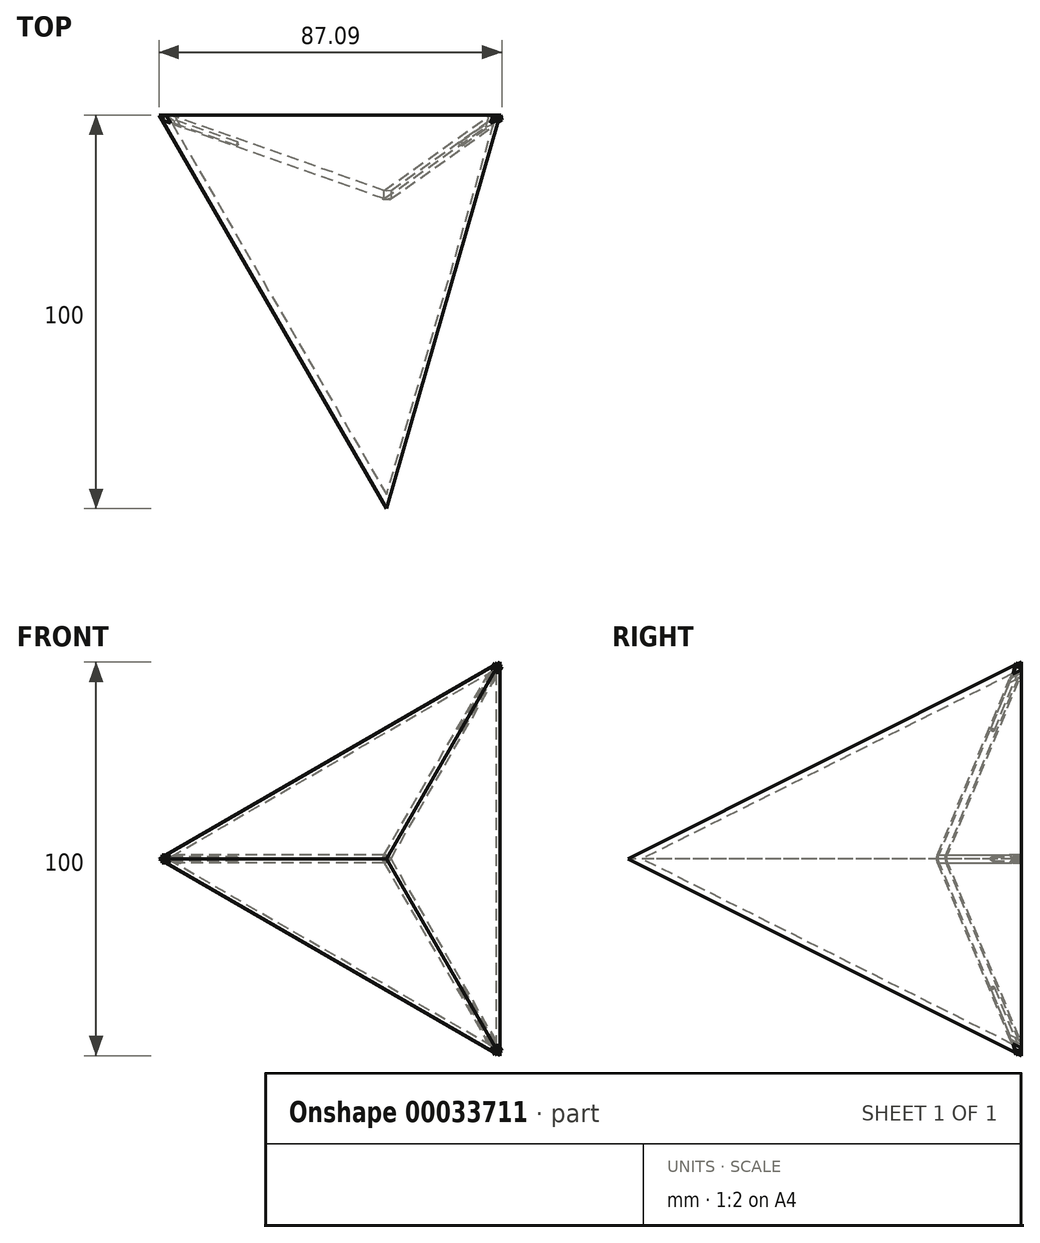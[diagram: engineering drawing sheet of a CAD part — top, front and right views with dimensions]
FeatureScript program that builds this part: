
annotation { "Feature Type Name" : "Feature", "Feature Type Description" : "" }
export const myFeature = defineFeature(function(context is Context, id is Id, definition is map)
    precondition{}
    {
        {
            var Q0;
            Q0=qCreatedBy(makeId("Front.planeOp"),FACE);
            var sketch = newSketch(context, id + "F0", { "sketchPlane" : qUnion([Q0])});
            skCircle(sketch, "E0.cCircle", {"center": v(0, 0) * mm, "radius": 28.87 * mm, "construction": true});
            skLineSegment(sketch, "E0.0", {"start": v(28.87, 50) * mm, "end": v(28.87, -50) * mm});
            skLineSegment(sketch, "E0.1", {"start": v(28.87, -50) * mm, "end": v(-57.74, 0) * mm});
            skLineSegment(sketch, "E0.2", {"start": v(-57.74, 0) * mm, "end": v(28.87, 50) * mm});
            skPoint(sketch, "E0.0.midPoint", {"position": v(28.87, 0) * mm});
            skSolve(sketch);
        }
        {
            var Q0;
            Q0=makeQuery(id+"F0.imprint","IMPRINT",FACE,{"disambiguationData":[TD([[makeQuery(id+"F0.imprint","IMPRINT",EDGE,{"derivedFrom":sQuery(id+"F0.wireOp",EDGE,"E0.0")}),-1.0]])]});
            cPlane(context, id + "F1", {"entities" : qUnion([Q0]), "cplaneType" : CPlaneType.OFFSET, "offset" : 100 * mm, "width" : 150 * mm, "height" : 150 * mm});
        }
        {
            var Q0;
            Q0=qCreatedBy(id+"F1.planeOp",FACE);
            var sketch = newSketch(context, id + "F2", { "sketchPlane" : qUnion([Q0])});
            skPoint(sketch, "E1", {"position": v(0, 0) * mm});
            skSolve(sketch);
        }
        {
            var Q0;
            Q0=makeQuery(id+"F0.imprint","IMPRINT",FACE,{"disambiguationData":[TD([[makeQuery(id+"F0.imprint","IMPRINT",EDGE,{"derivedFrom":sQuery(id+"F0.wireOp",EDGE,"E0.0")}),-1.0]])]});
            var Q1;
            Q1=sQuery(id+"F2.wireOp",VERTEX,"E1");
            loft(context, id + "F3", {"sheetProfilesArray" : [{ "sheetProfileEntities" : qUnion([Q0]) }, { "sheetProfileEntities" : qUnion([Q1]) }]});
        }
        {
            var Q0;
            Q0=makeQuery(id+"F3.opLoft","CAP_FACE",FACE,{"disambiguationData":[OSD([makeQuery(id+"F0.imprint","IMPRINT",FACE,{"disambiguationData":[TD([[makeQuery(id+"F0.imprint","IMPRINT",EDGE,{"derivedFrom":sQuery(id+"F0.wireOp",EDGE,"E0.0")}),-1.0]])]})])],"isStart":true});
            shell(context, id + "F4", {"entities" : qUnion([Q0]), "thickness" : 1 * mm});
        }
        {
            var Q0;
            Q0=qCreatedBy(makeId("Top.planeOp"),FACE);
            var sketch = newSketch(context, id + "F5", { "sketchPlane" : qUnion([Q0])});
            skLineSegment(sketch, "E2.0.0", {"start": v(-57.74, 0) * mm, "end": v(0, -100) * mm});
            skLineSegment(sketch, "E2.0.1", {"start": v(0, -100) * mm, "end": v(28.87, 0) * mm});
            skLineSegment(sketch, "E2.0.2", {"start": v(28.87, 0) * mm, "end": v(-57.74, 0) * mm});
            skLineSegment(sketch, "E3", {"start": v(0, -100) * mm, "end": v(0, 0) * mm});
            skLineSegment(sketch, "E4", {"start": v(-57.74, 0) * mm, "end": v(0, -20.45) * mm});
            skPoint(sketch, "E5", {"position": v(-57.74, 0) * mm});
            skLineSegment(sketch, "E6", {"start": v(0, -19.38) * mm, "end": v(-54.74, 0) * mm});
            skLineSegment(sketch, "E7", {"start": v(0, -21.5) * mm, "end": v(-56.97, -1.33) * mm});
            skSolve(sketch);
        }
        {
            var Q0;
            {var subQ0=sQuery(id+"F5.wireOp",EDGE,"E4");Q0=makeQuery(id+"F5.imprint","IMPRINT",FACE,{"disambiguationData":[TD([[makeQuery(id+"F5.imprint","IMPRINT",EDGE,{"derivedFrom":subQ0}),1.0]])]});}
            var Q1;
            {var subQ0=sQuery(id+"F5.wireOp",EDGE,"E4");Q1=makeQuery(id+"F5.imprint","IMPRINT",FACE,{"disambiguationData":[TD([[makeQuery(id+"F5.imprint","IMPRINT",EDGE,{"derivedFrom":subQ0}),-1.0]])]});}
            extrude(context, id + "F6", {"entities" : qUnion([Q0, Q1]), "operationType" : NewBodyOperationType.ADD, "depth" : 1 * mm, "hasSecondDirection" : true, "secondDirectionOppositeDirection" : true, "secondDirectionDepth" : 1 * mm});
        }
        {
            var Q0;
            {var subQ0=sQuery(id+"F5.wireOp",EDGE,"E2.0.2");var subQ1=sQuery(id+"F5.wireOp",EDGE,"E2.0.0");var subQ6=sQuery(id+"F5.wireOp",EDGE,"E7");Q0=makeQuery(id+"F6.boolean.opBoolean","SPLIT",FACE,{"disambiguationData":[TD([makeQuery(id+"F6.opExtrude","SWEPT_FACE",FACE,{"disambiguationData":[OSD([subQ1])]})])],"derivedFrom":makeQuery(id+"F6.opExtrude","CAP_FACE",FACE,{"disambiguationData":[OSD([subQ1,subQ0,sQuery(id+"F5.wireOp",EDGE,"E3"),sQuery(id+"F5.wireOp",EDGE,"E6"),subQ6])],"isStart":false})});}
            var sketch = newSketch(context, id + "F7", { "sketchPlane" : qUnion([Q0])});
            skLineSegment(sketch, "E8", {"start": v(-56.97, -1.33) * mm, "end": v(-56.5, 0) * mm});
            skLineSegment(sketch, "E9.0", {"start": v(0, -19.38) * mm, "end": v(-53.71, -0.36) * mm});
            skSolve(sketch);
        }
        {
            var Q0;
            {var subQ0=sQuery(id+"F7.wireOp",EDGE,"E8");Q0=makeQuery(id+"F7.imprint","IMPRINT",FACE,{"disambiguationData":[TD([[makeQuery(id+"F7.imprint","IMPRINT",EDGE,{"derivedFrom":subQ0}),1.0]])]});}
            extrude(context, id + "F8", {"entities" : qUnion([Q0]), "operationType" : NewBodyOperationType.REMOVE, "endBound" : BoundingType.THROUGH_ALL, "oppositeDirection" : true, "depth" : 25 * mm});
        }
        {
            var Q0;
            Q0=makeQuery(id+"F8.boolean.opBoolean","COPY",FACE,{"derivedFrom":makeQuery(id+"F8.opExtrude","SWEPT_FACE",FACE,{"disambiguationData":[OSD([sQuery(id+"F7.wireOp",EDGE,"E8")])]})});
            var sketch = newSketch(context, id + "F9", { "sketchPlane" : qUnion([Q0])});
            skLineSegment(sketch, "E10.0.0", {"start": v(20.27, -1) * mm, "end": v(20.27, 0) * mm});
            skLineSegment(sketch, "E10.0.1", {"start": v(20.27, 0) * mm, "end": v(20.27, 1) * mm});
            skLineSegment(sketch, "E10.0.2", {"start": v(20.27, 1) * mm, "end": v(18.86, 1) * mm});
            skLineSegment(sketch, "E10.0.3", {"start": v(18.86, 1) * mm, "end": v(18.86, -1) * mm});
            skLineSegment(sketch, "E10.0.4", {"start": v(18.86, -1) * mm, "end": v(20.27, -1) * mm});
            skPoint(sketch, "E11", {"position": v(19.57, 0) * mm});
            skSolve(sketch);
        }
        {
            var Q0;
            Q0=sQuery(id+"F9.wireOp",VERTEX,"E11");
            var Q1;
            Q1=makeQuery(id+"F3.opLoft","SWEPT_BODY",BODY,{"disambiguationData":[OSD([makeQuery(id+"F0.imprint","IMPRINT",FACE,{"disambiguationData":[TD([[makeQuery(id+"F0.imprint","IMPRINT",EDGE,{"derivedFrom":sQuery(id+"F0.wireOp",EDGE,"E0.0")}),-1.0]])]}),sQuery(id+"F2.wireOp",VERTEX,"E1")])]});
            hole(context, id + "F10", {"style" : HoleStyle.SIMPLE, "endStyle" : HoleEndStyle.BLIND, "holeDiameter" : 1 * mm, "holeDepth" : 20 * mm, "locations" : qUnion([Q0]), "scope" : qUnion([Q1])});
        }
        {
            var Q0;
            Q0=qCreatedBy(makeId("Top.planeOp"),FACE);
            var sketch = newSketch(context, id + "F11", { "sketchPlane" : qUnion([Q0])});
            skLineSegment(sketch, "E12", {"start": v(0, -99.77) * mm, "end": v(0, 0) * mm});
            skSolve(sketch);
        }
        {
            var Q0;
            Q0=makeQuery(id+"F3.opLoft","SWEPT_BODY",BODY,{"disambiguationData":[OSD([makeQuery(id+"F0.imprint","IMPRINT",FACE,{"disambiguationData":[TD([[makeQuery(id+"F0.imprint","IMPRINT",EDGE,{"derivedFrom":sQuery(id+"F0.wireOp",EDGE,"E0.0")}),-1.0]])]}),sQuery(id+"F2.wireOp",VERTEX,"E1")])]});
            var Q1;
            Q1=sQuery(id+"F11.wireOp",EDGE,"E12");
            circularPattern(context, id + "F12", {"entities" : qUnion([Q0]), "axis" : qUnion([Q1]), "angle" : 120 * degree, "instanceCount" : 2, "oppositeDirection" : true, "equalSpace" : true});
        }
        {
            var Q0;
            Q0=qCreatedBy(makeId("Top.planeOp"),FACE);
            var sketch = newSketch(context, id + "F13", { "sketchPlane" : qUnion([Q0])});
            skLineSegment(sketch, "E13", {"start": v(0, -100.39) * mm, "end": v(0, 0) * mm});
            skSolve(sketch);
        }
        {
            var Q0;
            Q0=makeQuery(id+"F3.opLoft","SWEPT_BODY",BODY,{"disambiguationData":[OSD([makeQuery(id+"F0.imprint","IMPRINT",FACE,{"disambiguationData":[TD([[makeQuery(id+"F0.imprint","IMPRINT",EDGE,{"derivedFrom":sQuery(id+"F0.wireOp",EDGE,"E0.0")}),-1.0]])]}),sQuery(id+"F2.wireOp",VERTEX,"E1")])]});
            var Q1;
            Q1=sQuery(id+"F13.wireOp",EDGE,"E13");
            circularPattern(context, id + "F14", {"operationType" : NewBodyOperationType.ADD, "entities" : qUnion([Q0]), "axis" : qUnion([Q1]), "angle" : 120 * degree, "instanceCount" : 2});
        }
    });
